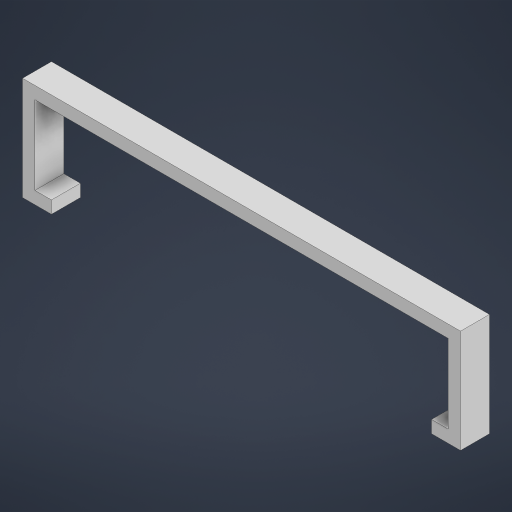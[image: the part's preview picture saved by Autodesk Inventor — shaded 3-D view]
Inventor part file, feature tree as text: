
AUTODESK INVENTOR PART (.ipt)
format: ipt  version: 2023 (Build 270158000, 158)  size: 195,584 bytes
history: native  units: in
note: dims shown in document units (in); Inventor stores cm internally (conversion verified against a paired STEP export)
features: sketch x4, extrude x3, other x1
ambient origin geometry x8: Origin, YZ Plane, XZ Plane, XY Plane, X Axis, Y Axis, Z Axis, Center Point
bodies: Body1 (feature_tree)
feature tree (8):
  other  "Bryła1"
  sketch  "Szkic1"
  extrude  "Wyciągnięcie proste1"  Depth=3.937in
  extrude  "Wyciągnięcie proste2"  Depth=0.2756in
  extrude  "Wyciągnięcie proste3"  Depth=0.1181in TaperAngle=0.0deg
  sketch  "Szkic2"
  sketch  "Szkic3"
  sketch  "Szkic4"
